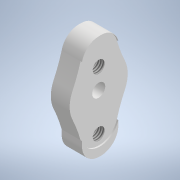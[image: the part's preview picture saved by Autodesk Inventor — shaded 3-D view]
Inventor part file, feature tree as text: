
AUTODESK INVENTOR PART (.ipt)
format: ipt  version: 2022 (Build 260153000, 153)  size: 174,080 bytes
history: native  units: mm
features: extrude x5, fillet x5, sketch x5, other x1, hole x1, projected_geometry x1
ambient origin geometry x8: Origin, YZ Plane, XZ Plane, XY Plane, X Axis, Y Axis, Z Axis, Center Point
bodies: Body1 (feature_tree)
feature tree (18):
  other  "ソリッド1"
  extrude  "押し出し1"  Depth=20.0mm
  extrude  "押し出し2"  Depth=5.5mm TaperAngle=0.0deg
  extrude  "押し出し3"  Depth=4.5mm
  fillet  "フィレット1"  [1 undecoded]
  hole  "穴1"  [1 undecoded]
  extrude  "押し出し4"  Depth=10.0mm TaperAngle=0.0deg
  fillet  "フィレット2"  Radius=50.0mm
  fillet  "フィレット3"  Radius=20.0mm
  extrude  "押し出し5"  Depth=7.0mm
  fillet  "フィレット4"  Radius=5.5mm
  fillet  "フィレット5"  Radius=6.0mm
  sketch  "スケッチ1"
  sketch  "スケッチ2"
  projected_geometry  "投影ループ1"
  sketch  "スケッチ4"
  sketch  "スケッチ6"
  sketch  "スケッチ7"
note: 2 required parameter values undecoded (feature->parameter linkage not recoverable at this tier; creation-order binding heuristic only, values carry confidence <= 0.55)
